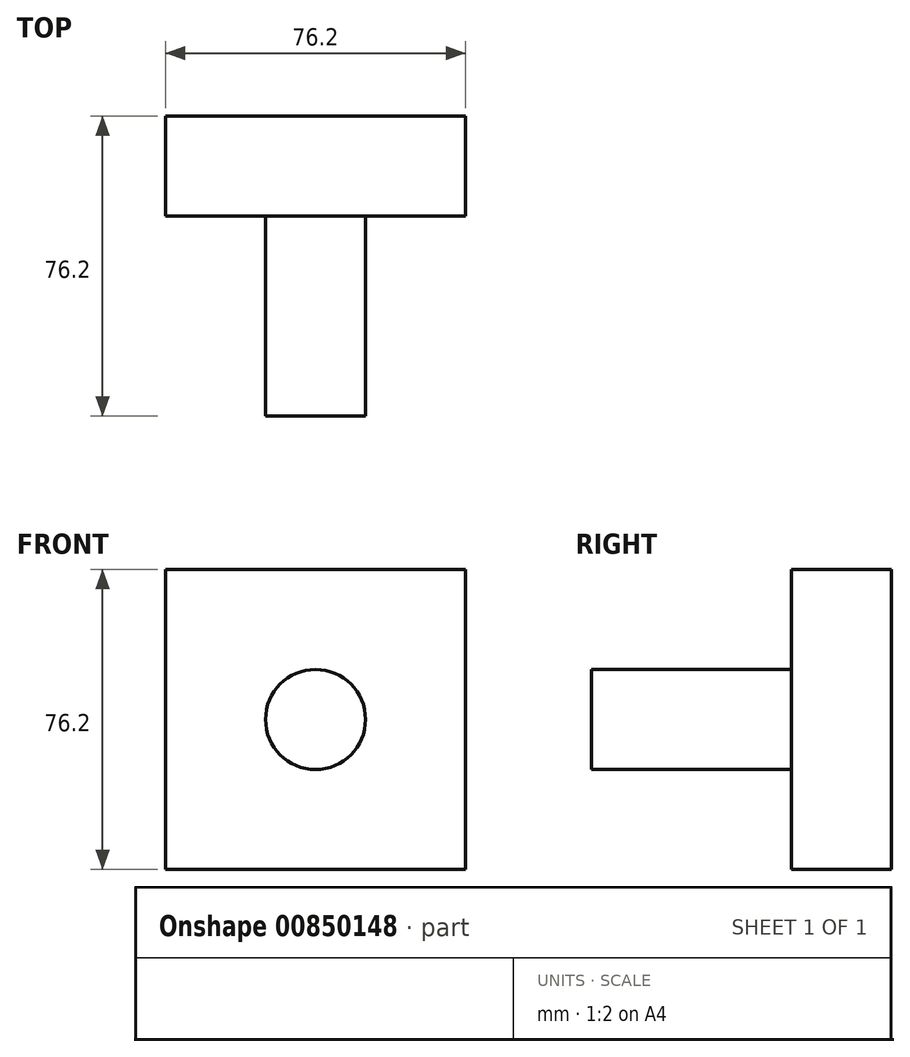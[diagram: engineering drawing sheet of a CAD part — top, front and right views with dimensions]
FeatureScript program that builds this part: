
annotation { "Feature Type Name" : "Feature", "Feature Type Description" : "" }
export const myFeature = defineFeature(function(context is Context, id is Id, definition is map)
    precondition{}
    {
        {
            var Q0;
            Q0=qCreatedBy(makeId("Front.planeOp"),FACE);
            var sketch = newSketch(context, id + "F0", { "sketchPlane" : qUnion([Q0])});
            skLineSegment(sketch, "E0.bottom", {"start": v(-38.1, 38.1) * mm, "end": v(38.1, 38.1) * mm});
            skLineSegment(sketch, "E0.top", {"start": v(-38.1, -38.1) * mm, "end": v(38.1, -38.1) * mm});
            skLineSegment(sketch, "E0.left", {"start": v(-38.1, 38.1) * mm, "end": v(-38.1, -38.1) * mm});
            skLineSegment(sketch, "E0.right", {"start": v(38.1, 38.1) * mm, "end": v(38.1, -38.1) * mm});
            skLineSegment(sketch, "E1", {"start": v(-38.1, 38.1) * mm, "end": v(38.1, -38.1) * mm, "construction": true});
            skSolve(sketch);
        }
        {
            var Q0;
            Q0=makeQuery(id+"F0.imprint","IMPRINT",FACE,{"disambiguationData":[TD([[makeQuery(id+"F0.imprint","IMPRINT",EDGE,{"derivedFrom":sQuery(id+"F0.wireOp",EDGE,"E0.bottom")}),-1.0]])]});
            extrude(context, id + "F1", {"entities" : qUnion([Q0]), "endBound" : BoundingType.SYMMETRIC, "depth" : 25.4 * mm, "offsetDistance" : 25.4 * mm});
        }
        {
            var Q0;
            Q0=makeQuery(id+"F1.opExtrude","CAP_FACE",FACE,{"disambiguationData":[OSD([sQuery(id+"F0.wireOp",EDGE,"E0.bottom"),sQuery(id+"F0.wireOp",EDGE,"E0.top"),sQuery(id+"F0.wireOp",EDGE,"E0.left"),sQuery(id+"F0.wireOp",EDGE,"E0.right")])],"isStart":false});
            var sketch = newSketch(context, id + "F2", { "sketchPlane" : qUnion([Q0])});
            skCircle(sketch, "E2", {"center": v(0, 0) * mm, "radius": 12.7 * mm});
            skSolve(sketch);
        }
        {
            var Q0;
            Q0 = qSketchRegion(id + "F2", true);
            extrude(context, id + "F3", {"entities" : qUnion([Q0]), "operationType" : NewBodyOperationType.ADD, "depth" : 50.8 * mm, "offsetDistance" : 25.4 * mm});
        }
    });
